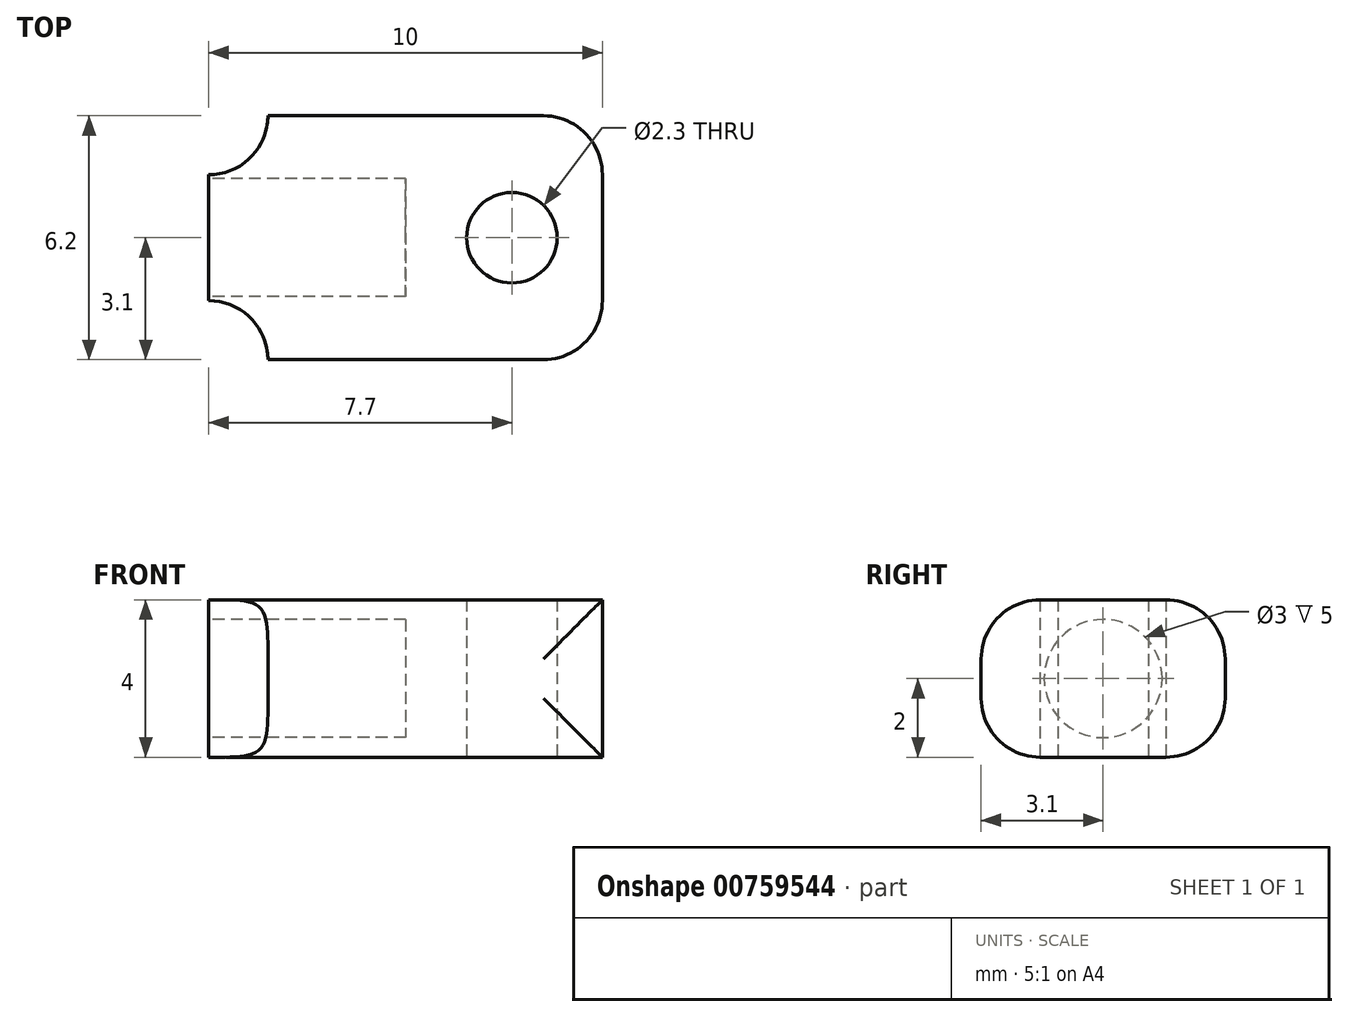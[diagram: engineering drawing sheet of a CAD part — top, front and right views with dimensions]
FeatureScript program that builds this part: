
annotation { "Feature Type Name" : "Feature", "Feature Type Description" : "" }
export const myFeature = defineFeature(function(context is Context, id is Id, definition is map)
    precondition{}
    {
        {
            var Q0;
            Q0=qCreatedBy(makeId("Top.planeOp"),FACE);
            var sketch = newSketch(context, id + "F0", { "sketchPlane" : qUnion([Q0])});
            skLineSegment(sketch, "E0.bottom", {"start": v(-3.5, 3.1) * mm, "end": v(5, 3.1) * mm});
            skLineSegment(sketch, "E0.top", {"start": v(-3.5, -3.1) * mm, "end": v(5, -3.1) * mm});
            skLineSegment(sketch, "E0.left", {"start": v(-5, 1.6) * mm, "end": v(-5, -1.6) * mm});
            skLineSegment(sketch, "E0.right", {"start": v(5, 3.1) * mm, "end": v(5, -3.1) * mm});
            skPoint(sketch, "E0.middle", {"position": v(0, 0) * mm});
            skArc(sketch, "E1", {"start": v(-5, 1.6) * mm, "mid": v(-3.94, 2.04) * mm, "end": v(-3.5, 3.1) * mm});
            skArc(sketch, "E2.MirrorCS", {"start": v(-5, -1.6) * mm, "mid": v(-3.94, -2.04) * mm, "end": v(-3.5, -3.1) * mm});
            skCircle(sketch, "E3", {"center": v(2.7, 0) * mm, "radius": 1.15 * mm});
            skSolve(sketch);
        }
        {
            var Q0;
            Q0 = qSketchRegion(id + "F0", true);
            extrude(context, id + "F1", {"entities" : qUnion([Q0]), "depth" : 4 * mm, "offsetDistance" : 25 * mm});
        }
        {
            var Q0;
            Q0=makeQuery(id+"F1.opExtrude","SWEPT_FACE",FACE,{"disambiguationData":[OSD([sQuery(id+"F0.wireOp",EDGE,"E0.left")])]});
            var sketch = newSketch(context, id + "F2", { "sketchPlane" : qUnion([Q0])});
            skCircle(sketch, "E4", {"center": v(0, 2) * mm, "radius": 1.5 * mm});
            skPoint(sketch, "E4.centerSnap0", {"position": v(-1.6, 2) * mm});
            skSolve(sketch);
        }
        {
            var Q0;
            Q0 = qSketchRegion(id + "F2", true);
            extrude(context, id + "F3", {"entities" : qUnion([Q0]), "operationType" : NewBodyOperationType.REMOVE, "oppositeDirection" : true, "depth" : 5 * mm, "offsetDistance" : 25 * mm});
        }
        {
            var Q0;
            Q0=makeQuery(id+"F1.opExtrude","CAP_EDGE",EDGE,{"disambiguationData":[OSD([sQuery(id+"F0.wireOp",EDGE,"E0.top")])],"isStart":false});
            var Q1;
            Q1=makeQuery(id+"F1.opExtrude","CAP_EDGE",EDGE,{"disambiguationData":[OSD([sQuery(id+"F0.wireOp",EDGE,"E0.bottom")])],"isStart":false});
            var Q2;
            Q2=makeQuery(id+"F1.opExtrude","SWEPT_EDGE",EDGE,{"disambiguationData":[OSD([sQuery(id+"F0.wireOp",EDGE,"E0.bottom"),sQuery(id+"F0.wireOp",EDGE,"E0.right")])]});
            var Q3;
            Q3=makeQuery(id+"F1.opExtrude","SWEPT_EDGE",EDGE,{"disambiguationData":[OSD([sQuery(id+"F0.wireOp",EDGE,"E0.top"),sQuery(id+"F0.wireOp",EDGE,"E0.right")])]});
            var Q4;
            Q4=makeQuery(id+"F1.opExtrude","CAP_EDGE",EDGE,{"disambiguationData":[OSD([sQuery(id+"F0.wireOp",EDGE,"E0.bottom")])],"isStart":true});
            var Q5;
            Q5=makeQuery(id+"F1.opExtrude","CAP_EDGE",EDGE,{"disambiguationData":[OSD([sQuery(id+"F0.wireOp",EDGE,"E0.top")])],"isStart":true});
            fillet(context, id + "F4", {"entities" : qUnion([Q0, Q1, Q2, Q3, Q4, Q5]), "radius" : 1.5 * mm, "tangentPropagation" : true, "allowEdgeOverflow" : false});
        }
    });
